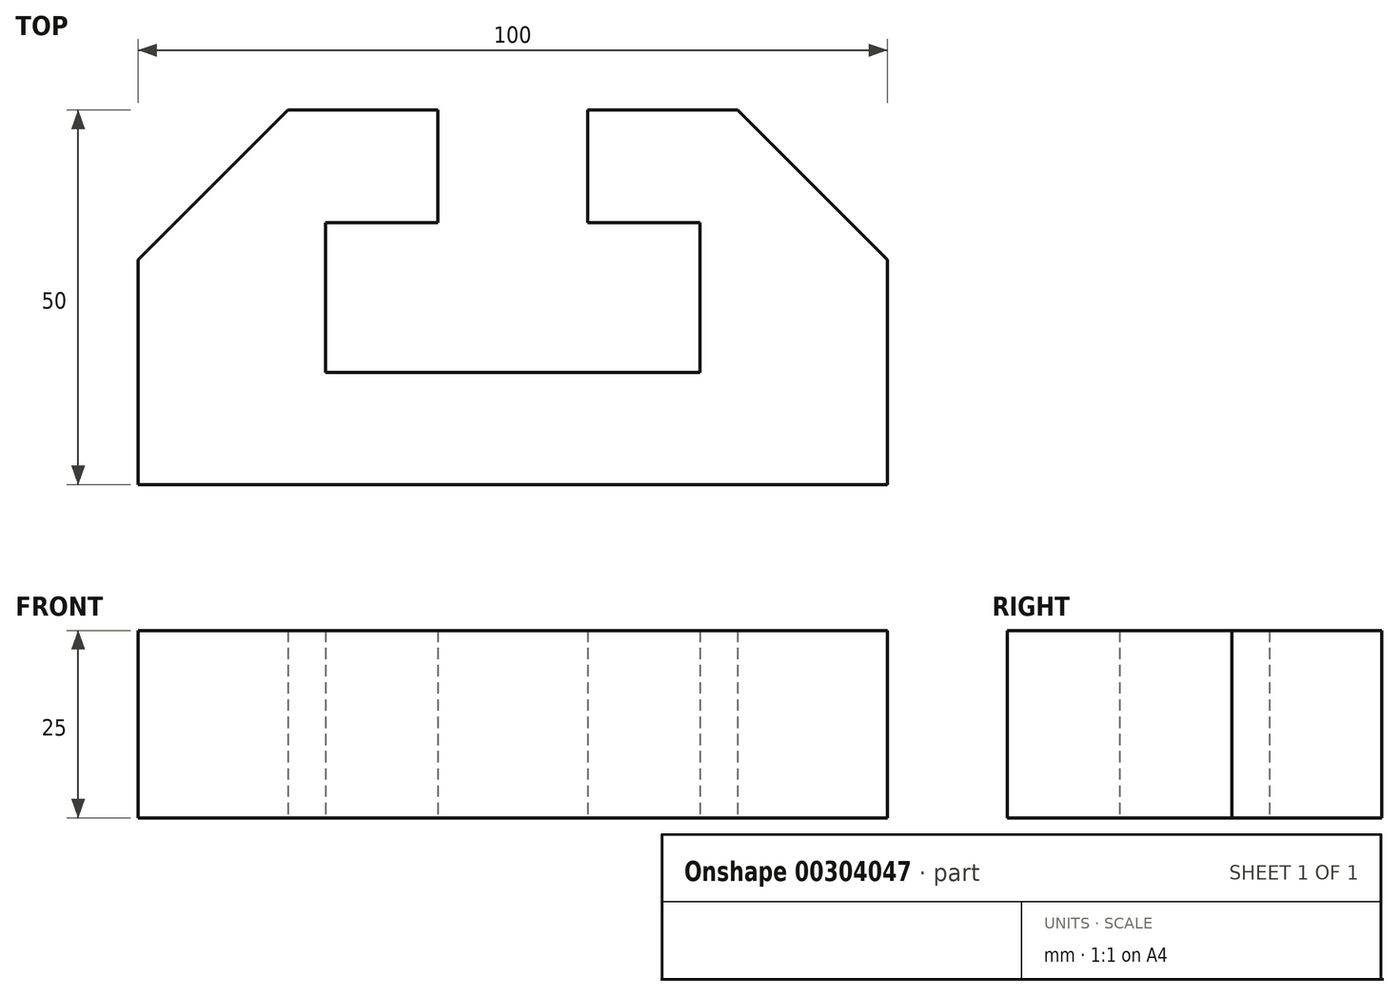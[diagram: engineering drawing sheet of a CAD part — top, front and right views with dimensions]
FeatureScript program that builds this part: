
annotation { "Feature Type Name" : "Feature", "Feature Type Description" : "" }
export const myFeature = defineFeature(function(context is Context, id is Id, definition is map)
    precondition{}
    {
        {
            var Q0;
            Q0=qCreatedBy(makeId("Top.planeOp"),FACE);
            var sketch = newSketch(context, id + "F0", { "sketchPlane" : qUnion([Q0])});
            skLineSegment(sketch, "E0", {"start": v(-57.86, -82.23) * mm, "end": v(42.14, -82.23) * mm});
            skLineSegment(sketch, "E1", {"start": v(42.14, -82.23) * mm, "end": v(42.14, -52.23) * mm});
            skLineSegment(sketch, "E2", {"start": v(-57.86, -82.23) * mm, "end": v(-57.86, -52.23) * mm});
            skLineSegment(sketch, "E3", {"start": v(42.14, -52.23) * mm, "end": v(22.14, -32.23) * mm});
            skLineSegment(sketch, "E4", {"start": v(-57.86, -52.23) * mm, "end": v(-37.86, -32.23) * mm});
            skLineSegment(sketch, "E5", {"start": v(-37.86, -32.23) * mm, "end": v(-17.86, -32.23) * mm});
            skLineSegment(sketch, "E6", {"start": v(-17.86, -32.23) * mm, "end": v(-17.86, -47.23) * mm});
            skLineSegment(sketch, "E7", {"start": v(22.14, -32.23) * mm, "end": v(2.14, -32.23) * mm});
            skLineSegment(sketch, "E8", {"start": v(2.14, -32.23) * mm, "end": v(2.14, -47.23) * mm});
            skLineSegment(sketch, "E9", {"start": v(-17.86, -47.23) * mm, "end": v(-32.86, -47.23) * mm});
            skLineSegment(sketch, "E10", {"start": v(2.14, -47.23) * mm, "end": v(17.14, -47.23) * mm});
            skLineSegment(sketch, "E11", {"start": v(17.14, -47.23) * mm, "end": v(17.14, -67.23) * mm});
            skLineSegment(sketch, "E12", {"start": v(-32.86, -47.23) * mm, "end": v(-32.86, -67.23) * mm});
            skLineSegment(sketch, "E13", {"start": v(-32.86, -67.23) * mm, "end": v(17.14, -67.23) * mm});
            skSolve(sketch);
        }
        {
            var Q0;
            Q0 = qSketchRegion(id + "F0", true);
            extrude(context, id + "F1", {"entities" : qUnion([Q0]), "depth" : 25 * mm});
        }
        {
            var Q0;
            Q0 = qSketchRegion(id + "F0", true);
            extrude(context, id + "F2", {"entities" : qUnion([Q0]), "operationType" : NewBodyOperationType.ADD, "depth" : 25 * mm});
        }
    });
